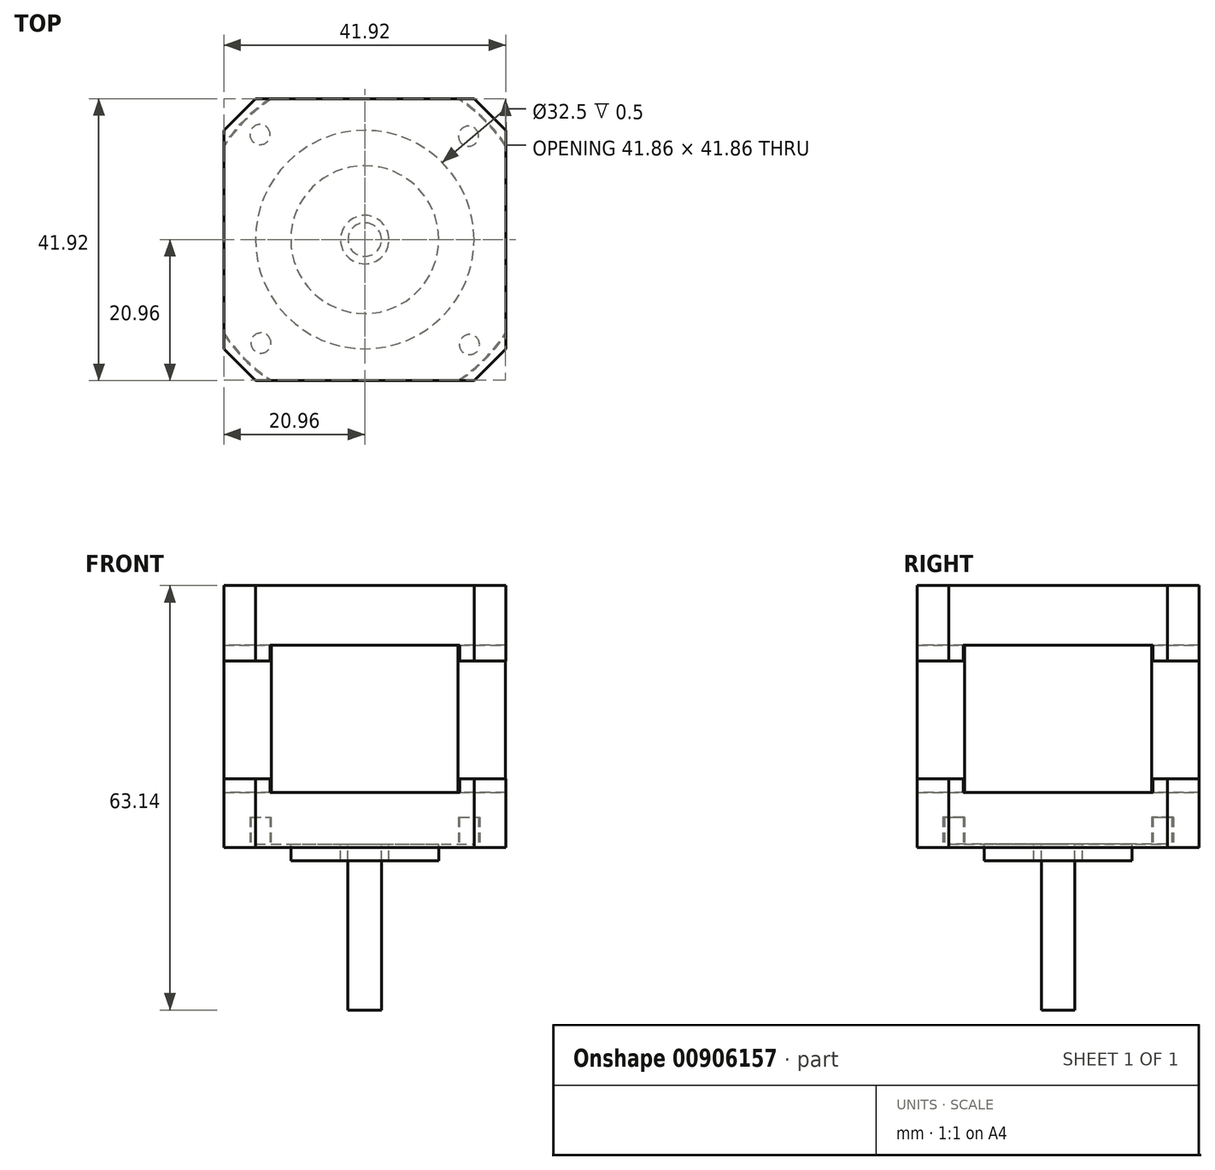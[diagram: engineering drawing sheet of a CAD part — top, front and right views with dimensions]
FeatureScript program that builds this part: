
annotation { "Feature Type Name" : "Feature", "Feature Type Description" : "" }
export const myFeature = defineFeature(function(context is Context, id is Id, definition is map)
    precondition{}
    {
        {
            var Q0;
            Q0=qCreatedBy(makeId("Top.planeOp"),FACE);
            var sketch = newSketch(context, id + "F0", { "sketchPlane" : qUnion([Q0])});
            skLineSegment(sketch, "E0", {"start": v(-20.96, 16.26) * mm, "end": v(-20.96, -16.26) * mm});
            skLineSegment(sketch, "E1", {"start": v(-20.96, -16.26) * mm, "end": v(-16.26, -20.96) * mm});
            skLineSegment(sketch, "E2", {"start": v(-16.26, -20.95) * mm, "end": v(16.26, -20.95) * mm});
            skLineSegment(sketch, "E3", {"start": v(16.26, -20.96) * mm, "end": v(20.96, -16.26) * mm});
            skLineSegment(sketch, "E4", {"start": v(20.96, -16.26) * mm, "end": v(20.96, 16.26) * mm});
            skLineSegment(sketch, "E5", {"start": v(20.95, 16.26) * mm, "end": v(16.26, 20.95) * mm});
            skLineSegment(sketch, "E6", {"start": v(16.26, 20.96) * mm, "end": v(-16.26, 20.96) * mm});
            skLineSegment(sketch, "E7", {"start": v(-16.26, 20.96) * mm, "end": v(-20.96, 16.26) * mm});
            skLineSegment(sketch, "E8", {"start": v(0, 20.96) * mm, "end": v(0, -20.95) * mm, "construction": true});
            skLineSegment(sketch, "E9", {"start": v(-20.96, 0) * mm, "end": v(20.96, 0) * mm, "construction": true});
            skLineSegment(sketch, "E10", {"start": v(18.6, 18.6) * mm, "end": v(-18.6, -18.6) * mm, "construction": true});
            skLineSegment(sketch, "E11", {"start": v(-18.6, 18.6) * mm, "end": v(18.6, -18.6) * mm, "construction": true});
            skSolve(sketch);
        }
        {
            var Q0;
            Q0 = qSketchRegion(id + "F0", true);
            extrude(context, id + "F1", {"entities" : qUnion([Q0]), "depth" : 11.23 * mm, "offsetDistance" : 25 * mm});
        }
        {
            var Q0;
            {var subQ0=sQuery(id+"F0.wireOp",EDGE,"E0");var subQ1=sQuery(id+"F0.wireOp",EDGE,"E1");var subQ2=sQuery(id+"F0.wireOp",EDGE,"E2");Q0=makeQuery(id+"F6.boolean.opBoolean","SPLIT",FACE,{"disambiguationData":[TD([makeQuery(id+"F1.opExtrude","SWEPT_FACE",FACE,{"disambiguationData":[OSD([subQ1])]})])],"derivedFrom":makeQuery(id+"F1.opExtrude","CAP_FACE",FACE,{"disambiguationData":[OSD([subQ0,subQ1,subQ2,sQuery(id+"F0.wireOp",EDGE,"E3"),sQuery(id+"F0.wireOp",EDGE,"E4"),sQuery(id+"F0.wireOp",EDGE,"E5"),sQuery(id+"F0.wireOp",EDGE,"E6"),sQuery(id+"F0.wireOp",EDGE,"E7")])],"isStart":true})});}
            cPlane(context, id + "F2", {"entities" : qUnion([Q0]), "cplaneType" : CPlaneType.OFFSET, "offset" : 17.53 * mm, "width" : 150 * mm, "height" : 150 * mm});
        }
        {
            var Q0;
            Q0=qCreatedBy(id+"F2.planeOp",FACE);
            var sketch = newSketch(context, id + "F3", { "sketchPlane" : qUnion([Q0])});
            skLineSegment(sketch, "E12", {"start": v(-20.96, 16.26) * mm, "end": v(-20.96, -16.26) * mm});
            skLineSegment(sketch, "E13", {"start": v(-20.96, -16.26) * mm, "end": v(-16.26, -20.96) * mm});
            skLineSegment(sketch, "E14", {"start": v(-16.26, -20.95) * mm, "end": v(16.26, -20.95) * mm});
            skLineSegment(sketch, "E15", {"start": v(16.26, -20.96) * mm, "end": v(20.96, -16.26) * mm});
            skLineSegment(sketch, "E16", {"start": v(20.96, -16.26) * mm, "end": v(20.96, 16.26) * mm});
            skLineSegment(sketch, "E17", {"start": v(20.96, 16.26) * mm, "end": v(16.26, 20.96) * mm});
            skLineSegment(sketch, "E18", {"start": v(16.26, 20.96) * mm, "end": v(-16.26, 20.96) * mm});
            skLineSegment(sketch, "E19", {"start": v(-16.26, 20.96) * mm, "end": v(-20.96, 16.26) * mm});
            skLineSegment(sketch, "E20", {"start": v(0, 20.96) * mm, "end": v(0, -20.95) * mm, "construction": true});
            skLineSegment(sketch, "E21", {"start": v(-20.96, 0) * mm, "end": v(20.96, 0) * mm, "construction": true});
            skLineSegment(sketch, "E22", {"start": v(18.6, 18.6) * mm, "end": v(-18.6, -18.6) * mm, "construction": true});
            skLineSegment(sketch, "E23", {"start": v(-18.6, 18.6) * mm, "end": v(18.6, -18.6) * mm, "construction": true});
            skSolve(sketch);
        }
        {
            var Q0;
            Q0=makeQuery(id+"F3.imprint","IMPRINT",FACE,{"disambiguationData":[TD([[makeQuery(id+"F3.imprint","IMPRINT",EDGE,{"derivedFrom":sQuery(id+"F3.wireOp",EDGE,"E12")}),1.0]])]});
            extrude(context, id + "F4", {"entities" : qUnion([Q0]), "operationType" : NewBodyOperationType.ADD, "depth" : 10.18 * mm, "offsetDistance" : 25 * mm});
        }
        {
            var Q0;
            Q0=makeQuery(id+"F1.opExtrude","CAP_FACE",FACE,{"disambiguationData":[OSD([sQuery(id+"F0.wireOp",EDGE,"E0"),sQuery(id+"F0.wireOp",EDGE,"E1"),sQuery(id+"F0.wireOp",EDGE,"E2"),sQuery(id+"F0.wireOp",EDGE,"E3"),sQuery(id+"F0.wireOp",EDGE,"E4"),sQuery(id+"F0.wireOp",EDGE,"E5"),sQuery(id+"F0.wireOp",EDGE,"E6"),sQuery(id+"F0.wireOp",EDGE,"E7")])],"isStart":true});
            var sketch = newSketch(context, id + "F5", { "sketchPlane" : qUnion([Q0])});
            skCircle(sketch, "E24", {"center": v(0, 0) * mm, "radius": 25.25 * mm});
            skSolve(sketch);
        }
        {
            var Q0;
            {var subQ0=sQuery(id+"F5.wireOp",EDGE,"E24");var subQ5=makeQuery(id+"F1.opExtrude","CAP_EDGE",EDGE,{"disambiguationData":[OSD([sQuery(id+"F0.wireOp",EDGE,"E2")])],"isStart":true});var subQ6=makeQuery(id+"F5.imprint","INTERSECT",VERTEX,{"disambiguationData":[OD(0.0)],"derivedFrom":[subQ5,subQ0]});Q0=makeQuery(id+"F5.imprint","IMPRINT",FACE,{"disambiguationData":[TD([[makeQuery(id+"F5.imprint","IMPRINT",EDGE,{"disambiguationData":[TD([[subQ6,1.0]])],"derivedFrom":subQ0}),1.0]])]});}
            extrude(context, id + "F6", {"entities" : qUnion([Q0]), "operationType" : NewBodyOperationType.REMOVE, "oppositeDirection" : true, "depth" : 2.36 * mm, "offsetDistance" : 25 * mm, "hasSecondDirection" : true, "secondDirectionOppositeDirection" : false, "secondDirectionDepth" : 19.56 * mm});
        }
        {
            var Q0;
            Q0=makeQuery(id+"F1.opExtrude","CAP_FACE",FACE,{"disambiguationData":[OSD([sQuery(id+"F0.wireOp",EDGE,"E0"),sQuery(id+"F0.wireOp",EDGE,"E1"),sQuery(id+"F0.wireOp",EDGE,"E2"),sQuery(id+"F0.wireOp",EDGE,"E3"),sQuery(id+"F0.wireOp",EDGE,"E4"),sQuery(id+"F0.wireOp",EDGE,"E5"),sQuery(id+"F0.wireOp",EDGE,"E6"),sQuery(id+"F0.wireOp",EDGE,"E7")])],"isStart":false});
            cPlane(context, id + "F7", {"entities" : qUnion([Q0]), "cplaneType" : CPlaneType.OFFSET, "offset" : 8.87 * mm, "oppositeDirection" : true, "width" : 150 * mm, "height" : 150 * mm});
        }
        {
            var Q0;
            Q0=qCreatedBy(id+"F7.planeOp",FACE);
            var sketch = newSketch(context, id + "F8", { "sketchPlane" : qUnion([Q0])});
            skLineSegment(sketch, "E25", {"start": v(-13.9, 20.93) * mm, "end": v(13.9, 20.93) * mm});
            skLineSegment(sketch, "E26", {"start": v(20.93, 13.9) * mm, "end": v(20.93, -13.9) * mm});
            skLineSegment(sketch, "E27", {"start": v(13.9, -20.93) * mm, "end": v(-13.9, -20.93) * mm});
            skLineSegment(sketch, "E28", {"start": v(-20.93, -13.9) * mm, "end": v(-20.93, 13.9) * mm});
            skLineSegment(sketch, "E29", {"start": v(0, 0) * mm, "end": v(0, 0) * mm});
            skLineSegment(sketch, "E30", {"start": v(0, 20.93) * mm, "end": v(0, -20.93) * mm, "construction": true});
            skLineSegment(sketch, "E31", {"start": v(-20.93, 0) * mm, "end": v(20.93, 0) * mm, "construction": true});
            skPoint(sketch, "E32", {"position": v(0, 0) * mm});
            skArc(sketch, "E33", {"start": v(-20.93, -13.9) * mm, "mid": v(-17.76, -17.76) * mm, "end": v(-13.9, -20.93) * mm});
            skArc(sketch, "E34.trimOffspring", {"start": v(13.9, -20.93) * mm, "mid": v(17.76, -17.76) * mm, "end": v(20.93, -13.9) * mm});
            skArc(sketch, "E35.trimOffspring", {"start": v(20.93, 13.9) * mm, "mid": v(17.76, 17.76) * mm, "end": v(13.9, 20.93) * mm});
            skArc(sketch, "E36.trimOffspring", {"start": v(-13.9, 20.93) * mm, "mid": v(-17.76, 17.76) * mm, "end": v(-20.93, 13.9) * mm});
            skSolve(sketch);
        }
        {
            var Q0;
            Q0 = qSketchRegion(id + "F8", true);
            extrude(context, id + "F9", {"entities" : qUnion([Q0]), "operationType" : NewBodyOperationType.ADD, "oppositeDirection" : true, "depth" : 21.92 * mm, "offsetDistance" : 25 * mm});
        }
        {
            var Q0;
            Q0=makeQuery(id+"F4.opExtrude","CAP_FACE",FACE,{"disambiguationData":[OSD([sQuery(id+"F3.wireOp",EDGE,"E12"),sQuery(id+"F3.wireOp",EDGE,"E13"),sQuery(id+"F3.wireOp",EDGE,"E14"),sQuery(id+"F3.wireOp",EDGE,"E15"),sQuery(id+"F3.wireOp",EDGE,"E16"),sQuery(id+"F3.wireOp",EDGE,"E17"),sQuery(id+"F3.wireOp",EDGE,"E18"),sQuery(id+"F3.wireOp",EDGE,"E19")])],"isStart":false});
            var sketch = newSketch(context, id + "F10", { "sketchPlane" : qUnion([Q0])});
            skCircle(sketch, "E37", {"center": v(0, 0) * mm, "radius": 16.25 * mm});
            skSolve(sketch);
        }
        {
            var Q0;
            Q0 = qSketchRegion(id + "F10", true);
            extrude(context, id + "F11", {"entities" : qUnion([Q0]), "operationType" : NewBodyOperationType.REMOVE, "oppositeDirection" : true, "depth" : .5 * mm, "offsetDistance" : 25 * mm});
        }
        {
            var Q0;
            Q0=makeQuery(id+"F11.boolean.opBoolean","COPY",FACE,{"derivedFrom":makeQuery(id+"F11.opExtrude","CAP_FACE",FACE,{"disambiguationData":[OSD([sQuery(id+"F10.wireOp",EDGE,"E37")])],"isStart":false})});
            var sketch = newSketch(context, id + "F12", { "sketchPlane" : qUnion([Q0])});
            skCircle(sketch, "E38", {"center": v(0, 0) * mm, "radius": 11 * mm});
            skCircle(sketch, "E39", {"center": v(0, 0) * mm, "radius": 3.6 * mm});
            skSolve(sketch);
        }
        {
            var Q0;
            Q0 = qSketchRegion(id + "F12", true);
            extrude(context, id + "F13", {"entities" : qUnion([Q0]), "operationType" : NewBodyOperationType.ADD, "depth" : 2.5 * mm, "offsetDistance" : 25 * mm});
        }
        {
            var Q0;
            Q0=makeQuery(id+"F13.boolean.opBoolean","SPLIT",FACE,{"disambiguationData":[TD([makeQuery(id+"F13.opExtrude","SWEPT_FACE",FACE,{"disambiguationData":[OSD([sQuery(id+"F12.wireOp",EDGE,"E39")])]})])],"derivedFrom":makeQuery(id+"F11.boolean.opBoolean","COPY",FACE,{"derivedFrom":makeQuery(id+"F11.opExtrude","CAP_FACE",FACE,{"disambiguationData":[OSD([sQuery(id+"F10.wireOp",EDGE,"E37")])],"isStart":false})})});
            var sketch = newSketch(context, id + "F14", { "sketchPlane" : qUnion([Q0])});
            skCircle(sketch, "E40", {"center": v(0, 0) * mm, "radius": 2.5 * mm});
            skSolve(sketch);
        }
        {
            var Q0;
            Q0 = qSketchRegion(id + "F14", true);
            extrude(context, id + "F15", {"entities" : qUnion([Q0]), "operationType" : NewBodyOperationType.ADD, "depth" : 24.7 * mm, "offsetDistance" : 25 * mm});
        }
        {
            var Q0;
            Q0=makeQuery(id+"F4.opExtrude","CAP_FACE",FACE,{"disambiguationData":[OSD([sQuery(id+"F3.wireOp",EDGE,"E12"),sQuery(id+"F3.wireOp",EDGE,"E13"),sQuery(id+"F3.wireOp",EDGE,"E14"),sQuery(id+"F3.wireOp",EDGE,"E15"),sQuery(id+"F3.wireOp",EDGE,"E16"),sQuery(id+"F3.wireOp",EDGE,"E17"),sQuery(id+"F3.wireOp",EDGE,"E18"),sQuery(id+"F3.wireOp",EDGE,"E19")])],"isStart":false});
            var sketch = newSketch(context, id + "F16", { "sketchPlane" : qUnion([Q0])});
            skCircle(sketch, "E41", {"center": v(15.43, -15.38) * mm, "radius": 1.5 * mm});
            skCircle(sketch, "E42", {"center": v(-15.57, -15.62) * mm, "radius": 1.5 * mm});
            skCircle(sketch, "E43", {"center": v(-15.43, 15.38) * mm, "radius": 1.5 * mm});
            skCircle(sketch, "E44", {"center": v(15.57, 15.62) * mm, "radius": 1.5 * mm});
            skLineSegment(sketch, "E45", {"start": v(15.57, 15.62) * mm, "end": v(-15.43, 15.38) * mm, "construction": true});
            skLineSegment(sketch, "E46", {"start": v(-15.43, 15.38) * mm, "end": v(-15.57, -15.62) * mm, "construction": true});
            skLineSegment(sketch, "E47", {"start": v(-15.57, -15.62) * mm, "end": v(15.43, -15.38) * mm, "construction": true});
            skLineSegment(sketch, "E48", {"start": v(15.43, -15.38) * mm, "end": v(15.57, 15.62) * mm, "construction": true});
            skLineSegment(sketch, "E49", {"start": v(15.43, -15.38) * mm, "end": v(-15.43, 15.38) * mm, "construction": true});
            skLineSegment(sketch, "E50", {"start": v(-15.57, -15.62) * mm, "end": v(15.57, 15.62) * mm, "construction": true});
            skSolve(sketch);
        }
        {
            var Q0;
            Q0 = qSketchRegion(id + "F16", true);
            extrude(context, id + "F17", {"entities" : qUnion([Q0]), "operationType" : NewBodyOperationType.REMOVE, "oppositeDirection" : true, "depth" : 4.5 * mm, "offsetDistance" : 25 * mm});
        }
    });
